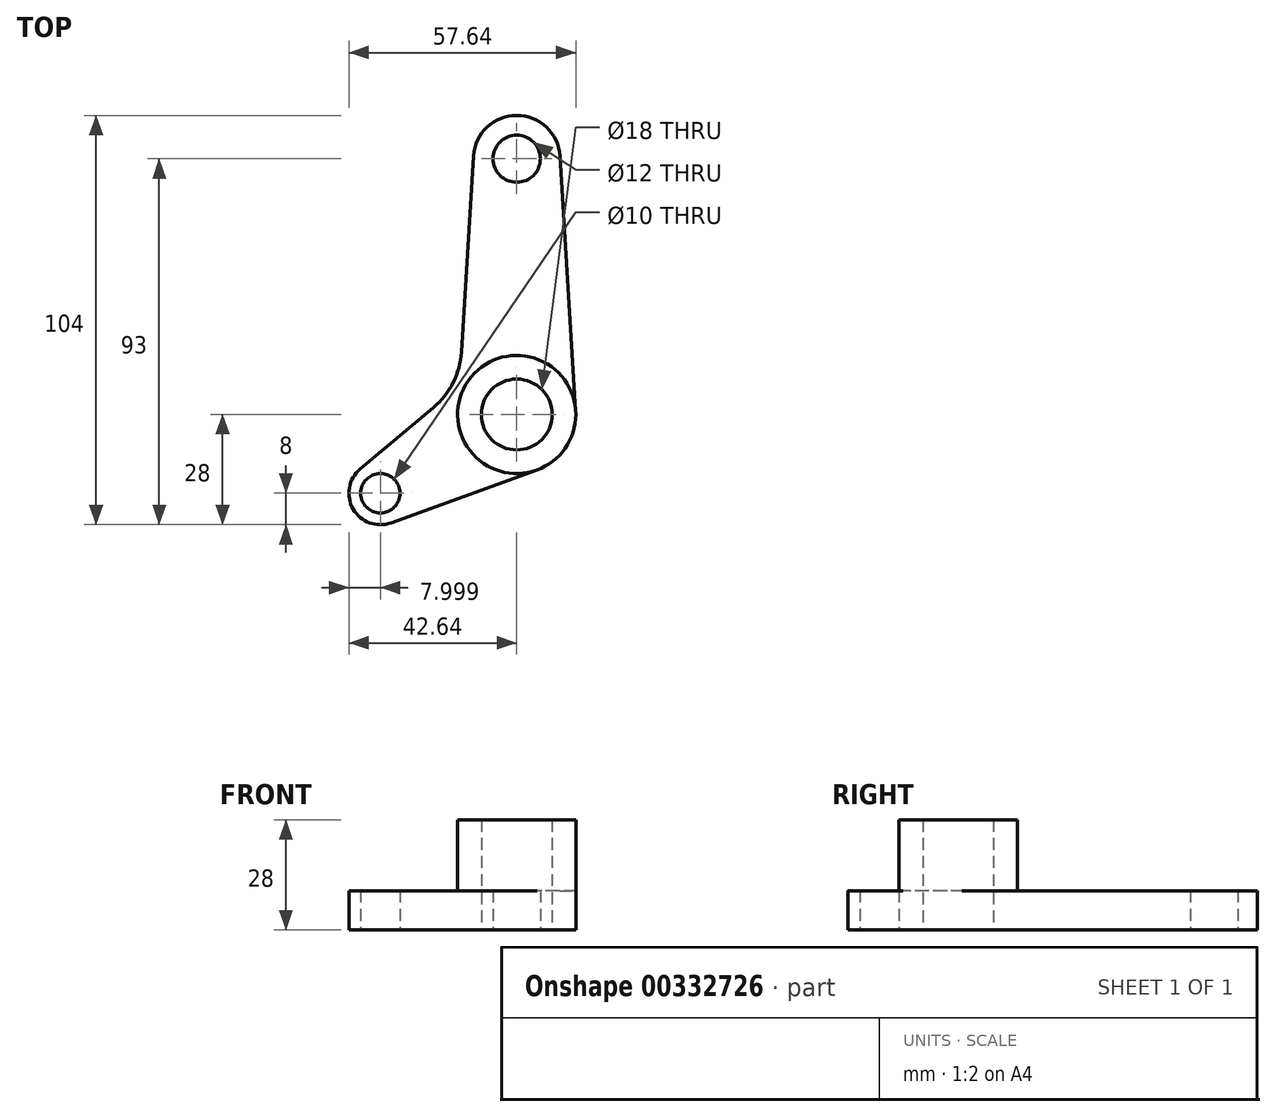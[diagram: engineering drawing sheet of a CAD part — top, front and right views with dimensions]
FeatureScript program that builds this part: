
annotation { "Feature Type Name" : "Feature", "Feature Type Description" : "" }
export const myFeature = defineFeature(function(context is Context, id is Id, definition is map)
    precondition{}
    {
        {
            var Q0;
            Q0=qCreatedBy(makeId("Top.planeOp"),FACE);
            var sketch = newSketch(context, id + "F0", { "sketchPlane" : qUnion([Q0])});
            skCircle(sketch, "E0", {"center": v(0, 0) * mm, "radius": 9 * mm});
            skCircle(sketch, "E1", {"center": v(0, 0) * mm, "radius": 15 * mm});
            skPoint(sketch, "E2", {"position": v(0, 65) * mm});
            skPoint(sketch, "E3", {"position": v(-34.64, -20) * mm});
            skCircle(sketch, "E4", {"center": v(-34.64, -20) * mm, "radius": 5 * mm});
            skArc(sketch, "E5", {"start": v(-39.8, -13.88) * mm, "mid": v(-41.57, -24) * mm, "end": v(-31.92, -27.52) * mm});
            skCircle(sketch, "E6", {"center": v(0, 65) * mm, "radius": 6 * mm});
            skArc(sketch, "E7", {"start": v(10.98, 65.68) * mm, "mid": v(0, 76) * mm, "end": v(-10.98, 65.68) * mm});
            skLineSegment(sketch, "E8", {"start": v(10.98, 65.68) * mm, "end": v(14.97, 0.92) * mm});
            skLineSegment(sketch, "E9", {"start": v(-31.92, -27.52) * mm, "end": v(5.11, -14.1) * mm});
            skLineSegment(sketch, "E10", {"start": v(-10.98, 65.68) * mm, "end": v(-14.05, 15.9) * mm});
            skArc(sketch, "E11", {"start": v(-21.13, 1.82) * mm, "mid": v(-16.15, 8.13) * mm, "end": v(-14.05, 15.9) * mm});
            skLineSegment(sketch, "E12.trimOffspring", {"start": v(-21.13, 1.82) * mm, "end": v(-39.8, -13.88) * mm});
            skSolve(sketch);
        }
        {
            var Q0;
            Q0=makeQuery(id+"F0.imprint","IMPRINT",FACE,{"disambiguationData":[TD([[makeQuery(id+"F0.imprint","IMPRINT",EDGE,{"derivedFrom":sQuery(id+"F0.wireOp",EDGE,"E0")}),-1.0]])]});
            extrude(context, id + "F1", {"entities" : qUnion([Q0]), "depth" : 28 * mm});
        }
        {
            var Q0;
            Q0 = qSketchRegion(id + "F0", true);
            extrude(context, id + "F2", {"entities" : qUnion([Q0]), "operationType" : NewBodyOperationType.ADD, "depth" : 10 * mm});
        }
    });
